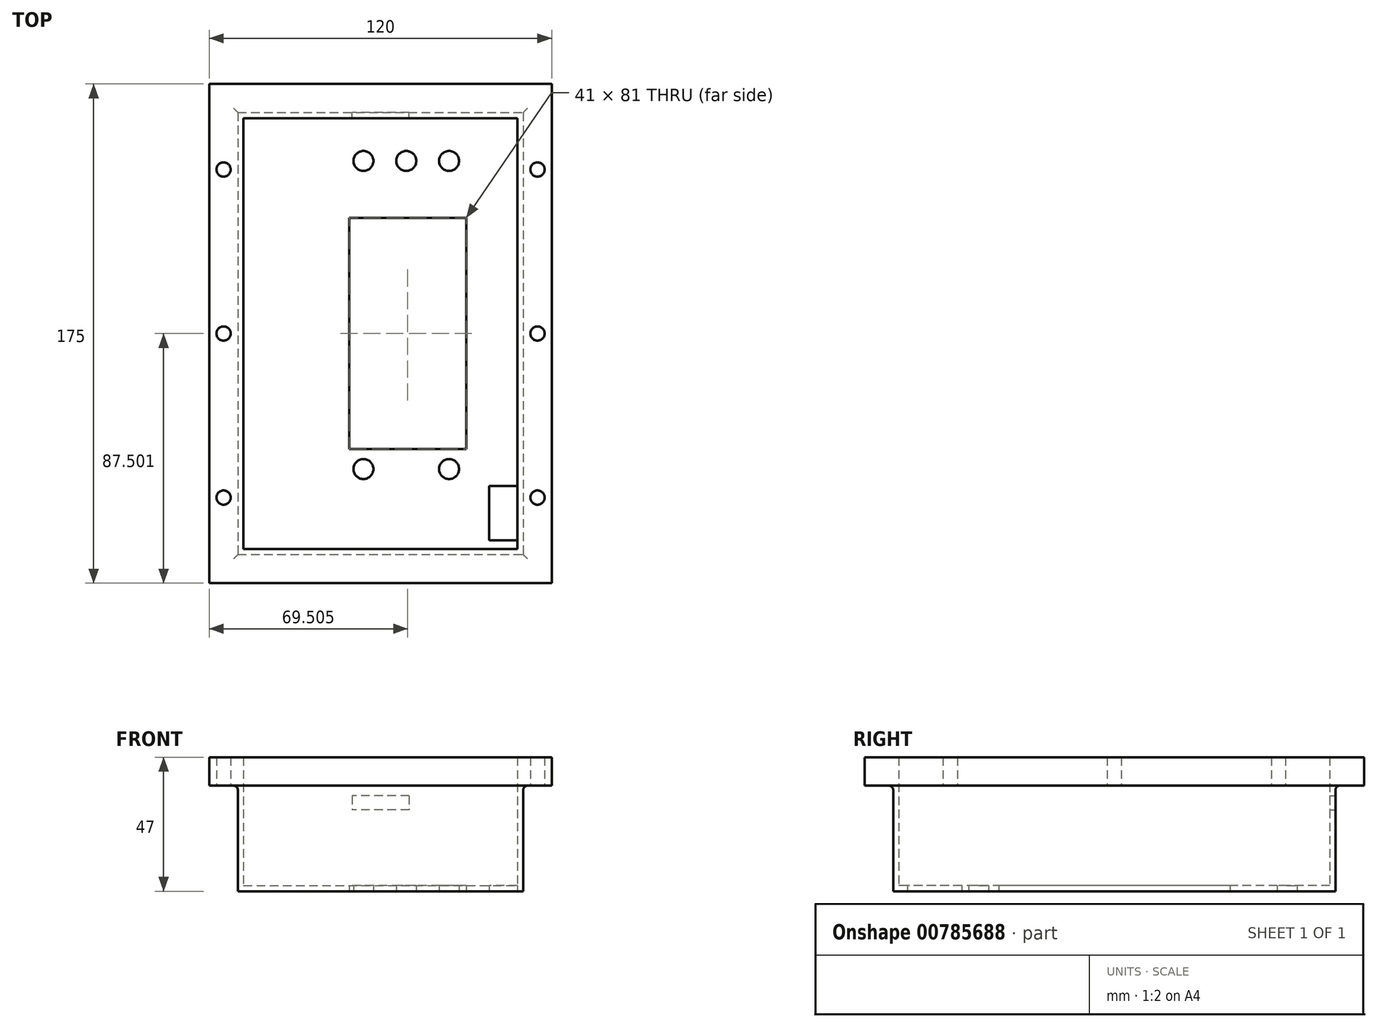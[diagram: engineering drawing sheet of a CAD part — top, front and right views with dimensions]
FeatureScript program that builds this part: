
annotation { "Feature Type Name" : "Feature", "Feature Type Description" : "" }
export const myFeature = defineFeature(function(context is Context, id is Id, definition is map)
    precondition{}
    {
        {
            var Q0;
            Q0=qCreatedBy(makeId("Top.planeOp"),FACE);
            var sketch = newSketch(context, id + "F0", { "sketchPlane" : qUnion([Q0])});
            skLineSegment(sketch, "E0.bottom", {"start": v(-46.69, 80.24) * mm, "end": v(53.31, 80.24) * mm});
            skLineSegment(sketch, "E0.top", {"start": v(-46.69, -74.76) * mm, "end": v(53.31, -74.76) * mm});
            skLineSegment(sketch, "E0.left", {"start": v(-46.69, 80.24) * mm, "end": v(-46.69, -74.76) * mm});
            skLineSegment(sketch, "E0.right", {"start": v(53.31, 80.24) * mm, "end": v(53.31, -74.76) * mm});
            skSolve(sketch);
        }
        {
            var Q0;
            Q0=makeQuery(id+"F0.imprint","IMPRINT",FACE,{"disambiguationData":[TD([[makeQuery(id+"F0.imprint","IMPRINT",EDGE,{"derivedFrom":sQuery(id+"F0.wireOp",EDGE,"E0.bottom")}),-1.0]])]});
            extrude(context, id + "F1", {"entities" : qUnion([Q0]), "depth" : 2 * mm, "offsetDistance" : 25 * mm});
        }
        {
            var Q0;
            Q0=makeQuery(id+"F1.opExtrude","CAP_FACE",FACE,{"disambiguationData":[OSD([sQuery(id+"F0.wireOp",EDGE,"E0.bottom"),sQuery(id+"F0.wireOp",EDGE,"E0.top"),sQuery(id+"F0.wireOp",EDGE,"E0.left"),sQuery(id+"F0.wireOp",EDGE,"E0.right")])],"isStart":false});
            var sketch = newSketch(context, id + "F2", { "sketchPlane" : qUnion([Q0])});
            skLineSegment(sketch, "E1.bottom", {"start": v(-46.69, 80.24) * mm, "end": v(53.31, 80.24) * mm});
            skLineSegment(sketch, "E1.top", {"start": v(-46.69, -74.76) * mm, "end": v(53.31, -74.76) * mm});
            skLineSegment(sketch, "E1.left", {"start": v(-46.69, 80.24) * mm, "end": v(-46.69, -74.76) * mm});
            skLineSegment(sketch, "E1.right", {"start": v(53.31, 80.24) * mm, "end": v(53.31, -74.76) * mm});
            skLineSegment(sketch, "E2.bottom", {"start": v(-44.69, 78.24) * mm, "end": v(51.31, 78.24) * mm});
            skLineSegment(sketch, "E2.top", {"start": v(-44.69, -72.76) * mm, "end": v(51.31, -72.76) * mm});
            skLineSegment(sketch, "E2.left", {"start": v(-44.69, 78.24) * mm, "end": v(-44.69, -72.76) * mm});
            skLineSegment(sketch, "E2.right", {"start": v(51.31, 78.24) * mm, "end": v(51.31, -72.76) * mm});
            skSolve(sketch);
        }
        {
            var Q0;
            Q0 = qSketchRegion(id + "F2", true);
            extrude(context, id + "F3", {"entities" : qUnion([Q0]), "operationType" : NewBodyOperationType.ADD, "depth" : 45 * mm, "offsetDistance" : 25 * mm});
        }
        {
            var Q0;
            Q0=makeQuery(id+"F1.opExtrude","CAP_FACE",FACE,{"disambiguationData":[OSD([sQuery(id+"F0.wireOp",EDGE,"E0.bottom"),sQuery(id+"F0.wireOp",EDGE,"E0.top"),sQuery(id+"F0.wireOp",EDGE,"E0.left"),sQuery(id+"F0.wireOp",EDGE,"E0.right")])],"isStart":true});
            var sketch = newSketch(context, id + "F4", { "sketchPlane" : qUnion([Q0])});
            skLineSegment(sketch, "E3.bottom", {"start": v(-7.69, 37.76) * mm, "end": v(33.31, 37.76) * mm});
            skLineSegment(sketch, "E3.top", {"start": v(-7.69, -43.24) * mm, "end": v(33.31, -43.24) * mm});
            skLineSegment(sketch, "E3.left", {"start": v(-7.69, 37.76) * mm, "end": v(-7.69, -43.24) * mm});
            skLineSegment(sketch, "E3.right", {"start": v(33.31, 37.76) * mm, "end": v(33.31, -43.24) * mm});
            skSolve(sketch);
        }
        {
            var Q0;
            Q0 = qSketchRegion(id + "F4", true);
            extrude(context, id + "F5", {"entities" : qUnion([Q0]), "operationType" : NewBodyOperationType.REMOVE, "oppositeDirection" : true, "depth" : 25 * mm, "offsetDistance" : 25 * mm});
        }
        {
            var Q0;
            Q0=makeQuery(id+"F1.opExtrude","CAP_FACE",FACE,{"disambiguationData":[OSD([sQuery(id+"F0.wireOp",EDGE,"E0.bottom"),sQuery(id+"F0.wireOp",EDGE,"E0.top"),sQuery(id+"F0.wireOp",EDGE,"E0.left"),sQuery(id+"F0.wireOp",EDGE,"E0.right")])],"isStart":true});
            var sketch = newSketch(context, id + "F6", { "sketchPlane" : qUnion([Q0])});
            skCircle(sketch, "E4", {"center": v(-2.69, 44.76) * mm, "radius": 3.5 * mm});
            skCircle(sketch, "E5", {"center": v(27.31, 44.76) * mm, "radius": 3.5 * mm});
            skCircle(sketch, "E6", {"center": v(-2.69, -63.24) * mm, "radius": 3.5 * mm});
            skCircle(sketch, "E7", {"center": v(12.31, -63.24) * mm, "radius": 3.5 * mm});
            skCircle(sketch, "E8", {"center": v(27.31, -63.24) * mm, "radius": 3.5 * mm});
            skSolve(sketch);
        }
        {
            var Q0;
            Q0=makeQuery(id+"F6.imprint","IMPRINT",FACE,{"disambiguationData":[TD([[makeQuery(id+"F6.imprint","IMPRINT",EDGE,{"derivedFrom":sQuery(id+"F6.wireOp",EDGE,"E4")}),1.0]])]});
            var Q1;
            Q1=makeQuery(id+"F6.imprint","IMPRINT",FACE,{"disambiguationData":[TD([[makeQuery(id+"F6.imprint","IMPRINT",EDGE,{"derivedFrom":sQuery(id+"F6.wireOp",EDGE,"E5")}),1.0]])]});
            var Q2;
            Q2=makeQuery(id+"F6.imprint","IMPRINT",FACE,{"disambiguationData":[TD([[makeQuery(id+"F6.imprint","IMPRINT",EDGE,{"derivedFrom":sQuery(id+"F6.wireOp",EDGE,"E8")}),1.0]])]});
            var Q3;
            Q3=makeQuery(id+"F6.imprint","IMPRINT",FACE,{"disambiguationData":[TD([[makeQuery(id+"F6.imprint","IMPRINT",EDGE,{"derivedFrom":sQuery(id+"F6.wireOp",EDGE,"E7")}),1.0]])]});
            var Q4;
            Q4=makeQuery(id+"F6.imprint","IMPRINT",FACE,{"disambiguationData":[TD([[makeQuery(id+"F6.imprint","IMPRINT",EDGE,{"derivedFrom":sQuery(id+"F6.wireOp",EDGE,"E6")}),1.0]])]});
            extrude(context, id + "F7", {"entities" : qUnion([Q0, Q1, Q2, Q3, Q4]), "operationType" : NewBodyOperationType.REMOVE, "oppositeDirection" : true, "depth" : 25 * mm, "offsetDistance" : 25 * mm});
        }
        {
            var Q0;
            Q0=makeQuery(id+"F1.opExtrude","CAP_FACE",FACE,{"disambiguationData":[OSD([sQuery(id+"F0.wireOp",EDGE,"E0.bottom"),sQuery(id+"F0.wireOp",EDGE,"E0.top"),sQuery(id+"F0.wireOp",EDGE,"E0.left"),sQuery(id+"F0.wireOp",EDGE,"E0.right")])],"isStart":true});
            var sketch = newSketch(context, id + "F8", { "sketchPlane" : qUnion([Q0])});
            skLineSegment(sketch, "E9.bottom", {"start": v(41.31, 69.76) * mm, "end": v(51.31, 69.76) * mm});
            skLineSegment(sketch, "E9.top", {"start": v(41.31, 50.76) * mm, "end": v(51.31, 50.76) * mm});
            skLineSegment(sketch, "E9.left", {"start": v(41.31, 69.76) * mm, "end": v(41.31, 50.76) * mm});
            skLineSegment(sketch, "E9.right", {"start": v(51.31, 69.76) * mm, "end": v(51.31, 50.76) * mm});
            skSolve(sketch);
        }
        {
            var Q0;
            Q0=makeQuery(id+"F8.imprint","IMPRINT",FACE,{"disambiguationData":[TD([[makeQuery(id+"F8.imprint","IMPRINT",EDGE,{"derivedFrom":sQuery(id+"F8.wireOp",EDGE,"E9.bottom")}),-1.0]])]});
            extrude(context, id + "F9", {"entities" : qUnion([Q0]), "operationType" : NewBodyOperationType.REMOVE, "oppositeDirection" : true, "depth" : 25 * mm, "offsetDistance" : 25 * mm});
        }
        {
            var Q0;
            Q0=makeQuery(id+"F3.opExtrude","CAP_FACE",FACE,{"disambiguationData":[OSD([sQuery(id+"F2.wireOp",EDGE,"E1.bottom"),sQuery(id+"F2.wireOp",EDGE,"E1.top"),sQuery(id+"F2.wireOp",EDGE,"E1.left"),sQuery(id+"F2.wireOp",EDGE,"E1.right"),sQuery(id+"F2.wireOp",EDGE,"E2.bottom"),sQuery(id+"F2.wireOp",EDGE,"E2.top"),sQuery(id+"F2.wireOp",EDGE,"E2.left"),sQuery(id+"F2.wireOp",EDGE,"E2.right")])],"isStart":false});
            var sketch = newSketch(context, id + "F10", { "sketchPlane" : qUnion([Q0])});
            skLineSegment(sketch, "E10.bottom", {"start": v(63.31, 90.24) * mm, "end": v(-56.69, 90.24) * mm});
            skLineSegment(sketch, "E10.top", {"start": v(63.31, -84.76) * mm, "end": v(-56.69, -84.76) * mm});
            skLineSegment(sketch, "E10.left", {"start": v(63.31, 90.24) * mm, "end": v(63.31, -84.76) * mm});
            skLineSegment(sketch, "E10.right", {"start": v(-56.69, 90.24) * mm, "end": v(-56.69, -84.76) * mm});
            skLineSegment(sketch, "E11.bottom", {"start": v(51.31, 78.24) * mm, "end": v(-44.69, 78.24) * mm});
            skLineSegment(sketch, "E11.top", {"start": v(51.31, -72.76) * mm, "end": v(-44.69, -72.76) * mm});
            skLineSegment(sketch, "E11.left", {"start": v(51.31, 78.24) * mm, "end": v(51.31, -72.76) * mm});
            skLineSegment(sketch, "E11.right", {"start": v(-44.69, 78.24) * mm, "end": v(-44.69, -72.76) * mm});
            skSolve(sketch);
        }
        {
            var Q0;
            Q0 = qSketchRegion(id + "F10", true);
            extrude(context, id + "F11", {"entities" : qUnion([Q0]), "operationType" : NewBodyOperationType.ADD, "oppositeDirection" : true, "depth" : 10 * mm, "offsetDistance" : 25 * mm});
        }
        {
            var Q0;
            Q0=makeQuery(id+"F11.opExtrude","CAP_FACE",FACE,{"disambiguationData":[OSD([sQuery(id+"F10.wireOp",EDGE,"E10.bottom"),sQuery(id+"F10.wireOp",EDGE,"E10.top"),sQuery(id+"F10.wireOp",EDGE,"E10.left"),sQuery(id+"F10.wireOp",EDGE,"E10.right"),sQuery(id+"F10.wireOp",EDGE,"E11.bottom"),sQuery(id+"F10.wireOp",EDGE,"E11.top"),sQuery(id+"F10.wireOp",EDGE,"E11.left"),sQuery(id+"F10.wireOp",EDGE,"E11.right")])],"isStart":false});
            var sketch = newSketch(context, id + "F12", { "sketchPlane" : qUnion([Q0])});
            skCircle(sketch, "E12", {"center": v(-51.69, -60.24) * mm, "radius": 2.5 * mm});
            skCircle(sketch, "E13", {"center": v(-51.69, -2.74) * mm, "radius": 2.5 * mm});
            skCircle(sketch, "E14", {"center": v(-51.69, 54.76) * mm, "radius": 2.5 * mm});
            skCircle(sketch, "E15", {"center": v(58.31, 54.76) * mm, "radius": 2.5 * mm});
            skCircle(sketch, "E16", {"center": v(58.31, -2.74) * mm, "radius": 2.5 * mm});
            skCircle(sketch, "E17", {"center": v(58.31, -60.24) * mm, "radius": 2.5 * mm});
            skSolve(sketch);
        }
        {
            var Q0;
            Q0 = qSketchRegion(id + "F12", true);
            extrude(context, id + "F13", {"entities" : qUnion([Q0]), "operationType" : NewBodyOperationType.REMOVE, "oppositeDirection" : true, "depth" : 25 * mm, "offsetDistance" : 25 * mm});
        }
        {
            var Q0;
            Q0=makeQuery(id+"F3.boolean.opBoolean","MERGE",FACE,{"derivedFrom":[makeQuery(id+"F1.opExtrude","SWEPT_FACE",FACE,{"disambiguationData":[OSD([sQuery(id+"F0.wireOp",EDGE,"E0.bottom")])]}),makeQuery(id+"F3.opExtrude","SWEPT_FACE",FACE,{"disambiguationData":[OSD([sQuery(id+"F2.wireOp",EDGE,"E1.bottom")])]})]});
            var sketch = newSketch(context, id + "F14", { "sketchPlane" : qUnion([Q0])});
            skLineSegment(sketch, "E18.bottom", {"start": v(-13.31, 33.49) * mm, "end": v(6.69, 33.49) * mm});
            skLineSegment(sketch, "E18.top", {"start": v(-13.31, 28.49) * mm, "end": v(6.69, 28.49) * mm});
            skLineSegment(sketch, "E18.left", {"start": v(-13.31, 33.49) * mm, "end": v(-13.31, 28.49) * mm});
            skLineSegment(sketch, "E18.right", {"start": v(6.69, 33.49) * mm, "end": v(6.69, 28.49) * mm});
            skSolve(sketch);
        }
        {
            var Q0;
            Q0 = qSketchRegion(id + "F14", true);
            extrude(context, id + "F15", {"entities" : qUnion([Q0]), "operationType" : NewBodyOperationType.REMOVE, "oppositeDirection" : true, "depth" : 25 * mm, "offsetDistance" : 25 * mm});
        }
        {
            var Q0;
            Q0=makeQuery(id+"F11.boolean.opBoolean","INTERSECT",EDGE,{"derivedFrom":[makeQuery(id+"F3.boolean.opBoolean","MERGE",FACE,{"derivedFrom":[makeQuery(id+"F1.opExtrude","SWEPT_FACE",FACE,{"disambiguationData":[OSD([sQuery(id+"F0.wireOp",EDGE,"E0.left")])]}),makeQuery(id+"F3.opExtrude","SWEPT_FACE",FACE,{"disambiguationData":[OSD([sQuery(id+"F2.wireOp",EDGE,"E1.left")])]})]}),makeQuery(id+"F11.opExtrude","CAP_FACE",FACE,{"disambiguationData":[OSD([sQuery(id+"F10.wireOp",EDGE,"E10.bottom"),sQuery(id+"F10.wireOp",EDGE,"E10.top"),sQuery(id+"F10.wireOp",EDGE,"E10.left"),sQuery(id+"F10.wireOp",EDGE,"E10.right"),sQuery(id+"F10.wireOp",EDGE,"E11.bottom"),sQuery(id+"F10.wireOp",EDGE,"E11.top"),sQuery(id+"F10.wireOp",EDGE,"E11.left"),sQuery(id+"F10.wireOp",EDGE,"E11.right")])],"isStart":false})]});
            var Q1;
            Q1=makeQuery(id+"F11.boolean.opBoolean","INTERSECT",EDGE,{"derivedFrom":[makeQuery(id+"F3.boolean.opBoolean","MERGE",FACE,{"derivedFrom":[makeQuery(id+"F1.opExtrude","SWEPT_FACE",FACE,{"disambiguationData":[OSD([sQuery(id+"F0.wireOp",EDGE,"E0.bottom")])]}),makeQuery(id+"F3.opExtrude","SWEPT_FACE",FACE,{"disambiguationData":[OSD([sQuery(id+"F2.wireOp",EDGE,"E1.bottom")])]})]}),makeQuery(id+"F11.opExtrude","CAP_FACE",FACE,{"disambiguationData":[OSD([sQuery(id+"F10.wireOp",EDGE,"E10.bottom"),sQuery(id+"F10.wireOp",EDGE,"E10.top"),sQuery(id+"F10.wireOp",EDGE,"E10.left"),sQuery(id+"F10.wireOp",EDGE,"E10.right"),sQuery(id+"F10.wireOp",EDGE,"E11.bottom"),sQuery(id+"F10.wireOp",EDGE,"E11.top"),sQuery(id+"F10.wireOp",EDGE,"E11.left"),sQuery(id+"F10.wireOp",EDGE,"E11.right")])],"isStart":false})]});
            var Q2;
            Q2=makeQuery(id+"F11.boolean.opBoolean","INTERSECT",EDGE,{"derivedFrom":[makeQuery(id+"F3.boolean.opBoolean","MERGE",FACE,{"derivedFrom":[makeQuery(id+"F1.opExtrude","SWEPT_FACE",FACE,{"disambiguationData":[OSD([sQuery(id+"F0.wireOp",EDGE,"E0.top")])]}),makeQuery(id+"F3.opExtrude","SWEPT_FACE",FACE,{"disambiguationData":[OSD([sQuery(id+"F2.wireOp",EDGE,"E1.top")])]})]}),makeQuery(id+"F11.opExtrude","CAP_FACE",FACE,{"disambiguationData":[OSD([sQuery(id+"F10.wireOp",EDGE,"E10.bottom"),sQuery(id+"F10.wireOp",EDGE,"E10.top"),sQuery(id+"F10.wireOp",EDGE,"E10.left"),sQuery(id+"F10.wireOp",EDGE,"E10.right"),sQuery(id+"F10.wireOp",EDGE,"E11.bottom"),sQuery(id+"F10.wireOp",EDGE,"E11.top"),sQuery(id+"F10.wireOp",EDGE,"E11.left"),sQuery(id+"F10.wireOp",EDGE,"E11.right")])],"isStart":false})]});
            var Q3;
            Q3=makeQuery(id+"F11.boolean.opBoolean","INTERSECT",EDGE,{"derivedFrom":[makeQuery(id+"F3.boolean.opBoolean","MERGE",FACE,{"derivedFrom":[makeQuery(id+"F1.opExtrude","SWEPT_FACE",FACE,{"disambiguationData":[OSD([sQuery(id+"F0.wireOp",EDGE,"E0.right")])]}),makeQuery(id+"F3.opExtrude","SWEPT_FACE",FACE,{"disambiguationData":[OSD([sQuery(id+"F2.wireOp",EDGE,"E1.right")])]})]}),makeQuery(id+"F11.opExtrude","CAP_FACE",FACE,{"disambiguationData":[OSD([sQuery(id+"F10.wireOp",EDGE,"E10.bottom"),sQuery(id+"F10.wireOp",EDGE,"E10.top"),sQuery(id+"F10.wireOp",EDGE,"E10.left"),sQuery(id+"F10.wireOp",EDGE,"E10.right"),sQuery(id+"F10.wireOp",EDGE,"E11.bottom"),sQuery(id+"F10.wireOp",EDGE,"E11.top"),sQuery(id+"F10.wireOp",EDGE,"E11.left"),sQuery(id+"F10.wireOp",EDGE,"E11.right")])],"isStart":false})]});
            fillet(context, id + "F16", {"entities" : qUnion([Q0, Q1, Q2, Q3]), "radius" : 1.5 * mm, "tangentPropagation" : true, "allowEdgeOverflow" : false});
        }
    });
